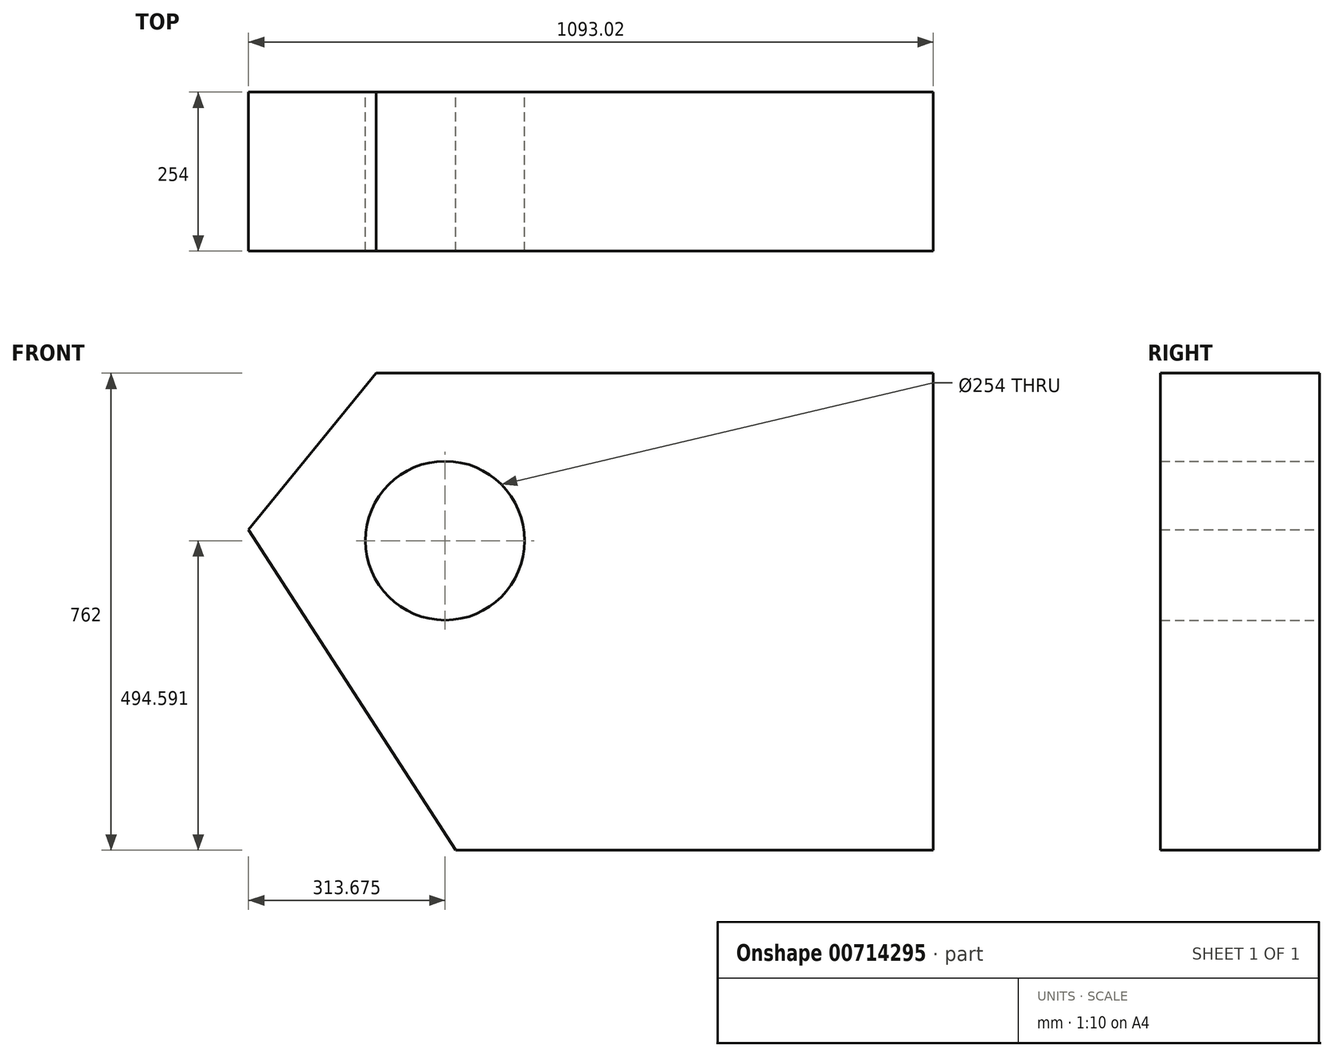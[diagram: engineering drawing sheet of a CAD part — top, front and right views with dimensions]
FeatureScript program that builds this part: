
annotation { "Feature Type Name" : "Feature", "Feature Type Description" : "" }
export const myFeature = defineFeature(function(context is Context, id is Id, definition is map)
    precondition{}
    {
        {
            var Q0;
            Q0=qCreatedBy(makeId("Front.planeOp"),FACE);
            var sketch = newSketch(context, id + "F0", { "sketchPlane" : qUnion([Q0])});
            skLineSegment(sketch, "E0", {"start": v(0, 0) * mm, "end": v(762, 0) * mm});
            skLineSegment(sketch, "E1", {"start": v(762, 0) * mm, "end": v(762, 762) * mm});
            skLineSegment(sketch, "E2", {"start": v(762, 762) * mm, "end": v(-127, 762) * mm});
            skLineSegment(sketch, "E3", {"start": v(0, 0) * mm, "end": v(-331.02, 511.9) * mm});
            skLineSegment(sketch, "E4", {"start": v(-127, 762) * mm, "end": v(-331.02, 511.9) * mm});
            skCircle(sketch, "E5", {"center": v(-17.34, 494.6) * mm, "radius": 127 * mm});
            skSolve(sketch);
        }
        {
            var Q0;
            Q0 = qSketchRegion(id + "F0", true);
            extrude(context, id + "F1", {"entities" : qUnion([Q0]), "depth" : 254 * mm, "offsetDistance" : 25.4 * mm});
        }
    });
